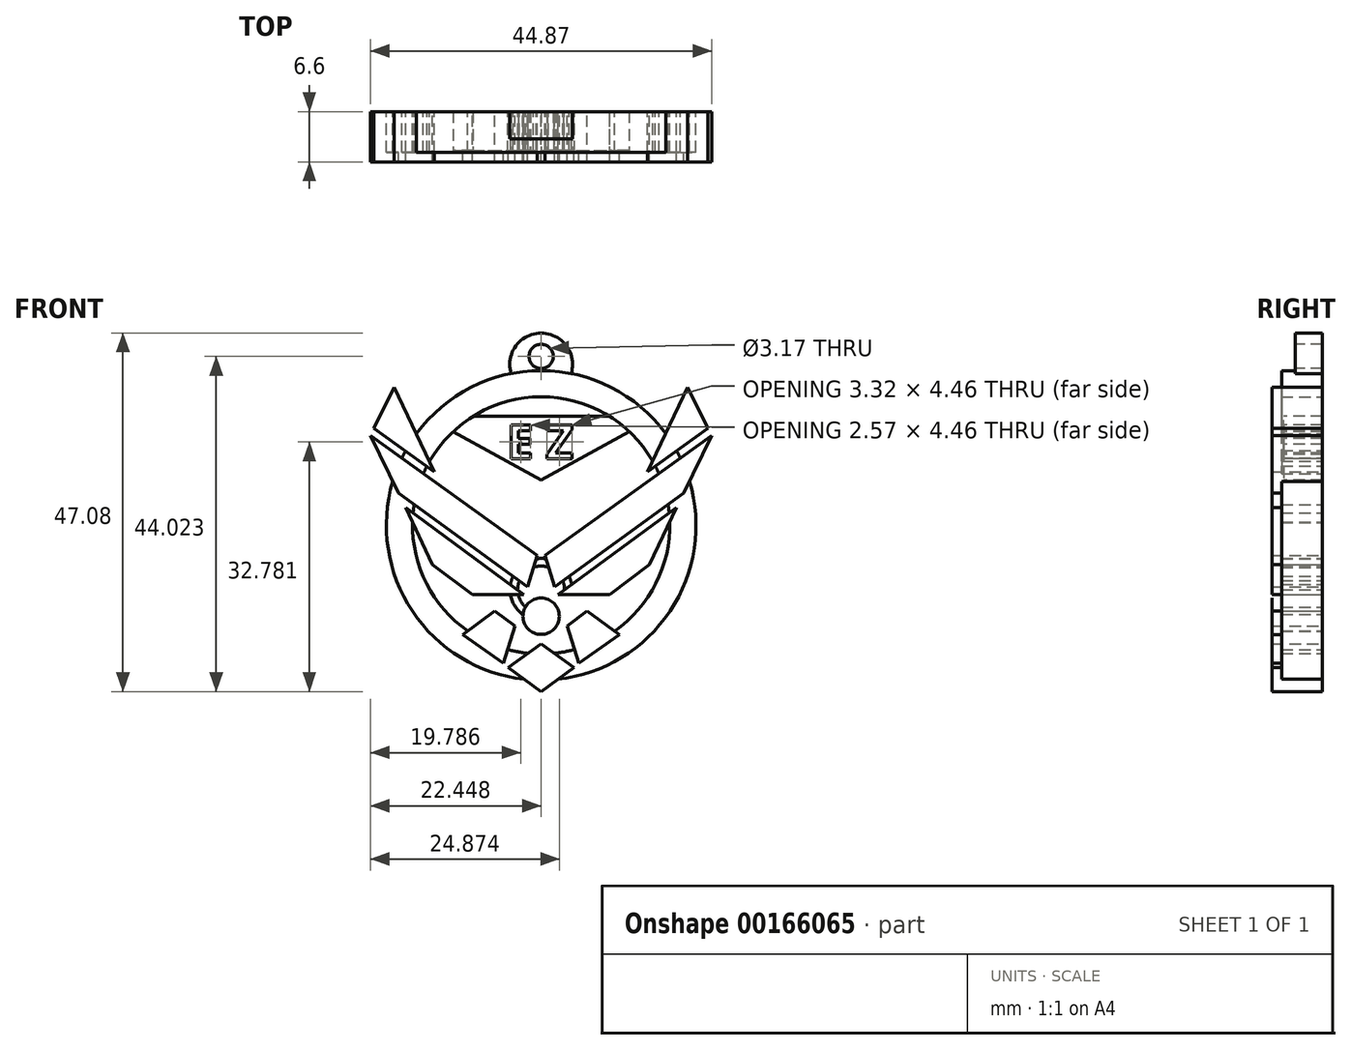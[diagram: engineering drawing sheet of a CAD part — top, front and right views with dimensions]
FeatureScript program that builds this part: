
annotation { "Feature Type Name" : "Feature", "Feature Type Description" : "" }
export const myFeature = defineFeature(function(context is Context, id is Id, definition is map)
    precondition{}
    {
        {
            var Q0;
            Q0=qCreatedBy(makeId("Front.planeOp"),FACE);
            var sketch = newSketch(context, id + "F0", { "sketchPlane" : qUnion([Q0])});
            skLineSegment(sketch, "E0", {"start": v(-11.75, -13.54) * mm, "end": v(-7.45, -10.45) * mm});
            skLineSegment(sketch, "E1", {"start": v(-11.75, -13.54) * mm, "end": v(-7.45, -16.7) * mm});
            skArc(sketch, "E2", {"start": v(-7.43, -4.4) * mm, "mid": v(-9.82, -6.8) * mm, "end": v(-7.43, -9.2) * mm});
            skLineSegment(sketch, "E3", {"start": v(-13.5, -6.12) * mm, "end": v(-10.86, -8.08) * mm});
            skLineSegment(sketch, "E4", {"start": v(-10.86, -8.08) * mm, "end": v(-12.4, -12.94) * mm});
            skLineSegment(sketch, "E5", {"start": v(-12.4, -12.94) * mm, "end": v(-17.74, -9.24) * mm});
            skLineSegment(sketch, "E6", {"start": v(-17.74, -9.24) * mm, "end": v(-13.5, -6.12) * mm});
            skLineSegment(sketch, "E7", {"start": v(-25.25, 7.48) * mm, "end": v(-21.7, 0) * mm});
            skLineSegment(sketch, "E8", {"start": v(-21.7, 0) * mm, "end": v(-16.47, -3.95) * mm});
            skLineSegment(sketch, "E9", {"start": v(-16.47, -3.95) * mm, "end": v(-9.7, -3.95) * mm});
            skLineSegment(sketch, "E10", {"start": v(-9.7, -3.95) * mm, "end": v(-25.25, 7.48) * mm});
            skLineSegment(sketch, "E11", {"start": v(-29.88, 16.94) * mm, "end": v(-7.95, 1.18) * mm});
            skLineSegment(sketch, "E12", {"start": v(-7.95, 1.18) * mm, "end": v(-9.22, -2.92) * mm});
            skLineSegment(sketch, "E13", {"start": v(-9.22, -2.92) * mm, "end": v(-26.2, 9.35) * mm});
            skLineSegment(sketch, "E14", {"start": v(-26.2, 9.35) * mm, "end": v(-29.88, 16.94) * mm});
            skLineSegment(sketch, "E15", {"start": v(-29.39, 17.92) * mm, "end": v(-21.44, 12.2) * mm});
            skLineSegment(sketch, "E16", {"start": v(-21.44, 12.2) * mm, "end": v(-26.72, 23.3) * mm});
            skLineSegment(sketch, "E17", {"start": v(-26.72, 23.3) * mm, "end": v(-29.39, 17.92) * mm});
            skArc(sketch, "E18.MirrorCS", {"start": v(-7.45, -4.4) * mm, "mid": v(-5.05, -6.8) * mm, "end": v(-7.45, -9.2) * mm});
            skLineSegment(sketch, "E19.MirrorCS", {"start": v(-3.14, -13.54) * mm, "end": v(-7.45, -10.45) * mm});
            skLineSegment(sketch, "E20.MirrorCS", {"start": v(-3.14, -13.54) * mm, "end": v(-7.45, -16.7) * mm});
            skLineSegment(sketch, "E21.MirrorCS", {"start": v(-5.67, -2.92) * mm, "end": v(11.3, 9.35) * mm});
            skLineSegment(sketch, "E22.MirrorCS", {"start": v(14.5, 17.92) * mm, "end": v(6.55, 12.2) * mm});
            skLineSegment(sketch, "E23.MirrorCS", {"start": v(11.83, 23.3) * mm, "end": v(14.5, 17.92) * mm});
            skLineSegment(sketch, "E24.MirrorCS", {"start": v(10.36, 7.48) * mm, "end": v(6.81, 0) * mm});
            skLineSegment(sketch, "E25.MirrorCS", {"start": v(2.85, -9.24) * mm, "end": v(-1.39, -6.12) * mm});
            skLineSegment(sketch, "E26.MirrorCS", {"start": v(-2.5, -12.94) * mm, "end": v(2.85, -9.24) * mm});
            skLineSegment(sketch, "E27.MirrorCS", {"start": v(-4.03, -8.08) * mm, "end": v(-2.5, -12.94) * mm});
            skLineSegment(sketch, "E28.MirrorCS", {"start": v(-1.39, -6.12) * mm, "end": v(-4.03, -8.08) * mm});
            skLineSegment(sketch, "E29.MirrorCS", {"start": v(-5.2, -3.95) * mm, "end": v(10.36, 7.48) * mm});
            skLineSegment(sketch, "E30.MirrorCS", {"start": v(1.58, -3.95) * mm, "end": v(-5.2, -3.95) * mm});
            skLineSegment(sketch, "E31.MirrorCS", {"start": v(6.81, 0) * mm, "end": v(1.58, -3.95) * mm});
            skLineSegment(sketch, "E32.MirrorCS", {"start": v(6.55, 12.2) * mm, "end": v(11.83, 23.3) * mm});
            skLineSegment(sketch, "E33.MirrorCS", {"start": v(11.3, 9.35) * mm, "end": v(14.99, 16.94) * mm});
            skLineSegment(sketch, "E34.MirrorCS", {"start": v(14.99, 16.94) * mm, "end": v(-6.94, 1.18) * mm});
            skLineSegment(sketch, "E35.MirrorCS", {"start": v(-6.94, 1.18) * mm, "end": v(-5.67, -2.92) * mm});
            skCircle(sketch, "E36", {"center": v(-7.43, 5.14) * mm, "radius": 20.33 * mm});
            skCircle(sketch, "E37", {"center": v(-7.43, 5.14) * mm, "radius": 16.9 * mm});
            skCircle(sketch, "E38", {"center": v(-7.44, -3.28) * mm, "radius": 4.07 * mm});
            skCircle(sketch, "E39", {"center": v(-7.44, -3.28) * mm, "radius": 3.07 * mm});
            skCircle(sketch, "E40", {"center": v(-7.43, 26.27) * mm, "radius": 4.13 * mm});
            skCircle(sketch, "E41", {"center": v(-7.43, 27.33) * mm, "radius": 1.59 * mm});
            skText(sketch, "E42", { "text": "E Z", "fontName": "OpenSans-Bold.ttf"});
            skLineSegment(sketch, "E43", {"start": v(-7.44, 18.9) * mm, "end": v(-7.44, 13.47) * mm});
            skLineSegment(sketch, "E44", {"start": v(-19, 17.46) * mm, "end": v(-7.44, 11.07) * mm});
            skLineSegment(sketch, "E45", {"start": v(-7.44, 11.07) * mm, "end": v(4.13, 17.46) * mm});
            skLineSegment(sketch, "E46", {"start": v(-16.38, 19.47) * mm, "end": v(1.52, 19.47) * mm});
            const initialGuessF0  = {"E42": [-0.01194, 0.01386, 1, 0, 0.0045]};
            skSetInitialGuess(sketch, initialGuessF0);
            skSolve(sketch);
        }
        {
            var Q0;
            {var subQ0=sQuery(id+"F0.wireOp",EDGE,"E17");Q0=makeQuery(id+"F0.imprint","IMPRINT",FACE,{"disambiguationData":[TD([[makeQuery(id+"F0.imprint","IMPRINT",EDGE,{"derivedFrom":subQ0}),1.0]])]});}
            var Q1;
            {var subQ0=sQuery(id+"F0.wireOp",EDGE,"E36");var subQ1=sQuery(id+"F0.wireOp",EDGE,"E15");var subQ2=makeQuery(id+"F0.imprint","INTERSECT",VERTEX,{"derivedFrom":[subQ1,subQ0]});Q1=makeQuery(id+"F0.imprint","IMPRINT",FACE,{"disambiguationData":[TD([[makeQuery(id+"F0.imprint","IMPRINT",EDGE,{"disambiguationData":[TD([[subQ2,-1.0]])],"derivedFrom":subQ1}),1.0]])]});}
            var Q2;
            {var subQ0=sQuery(id+"F0.wireOp",EDGE,"E16");var subQ1=sQuery(id+"F0.wireOp",EDGE,"E15");var subQ2=makeQuery(id+"F0.imprint","INTERSECT",VERTEX,{"derivedFrom":[subQ1,subQ0]});Q2=makeQuery(id+"F0.imprint","IMPRINT",FACE,{"disambiguationData":[TD([[makeQuery(id+"F0.imprint","IMPRINT",EDGE,{"disambiguationData":[TD([[subQ2,1.0]])],"derivedFrom":subQ1}),1.0]])]});}
            var Q3;
            {var subQ1=sQuery(id+"F0.wireOp",EDGE,"E11");var subQ7=sQuery(id+"F0.wireOp",EDGE,"E36");var subQ9=makeQuery(id+"F0.imprint","INTERSECT",VERTEX,{"derivedFrom":[subQ1,subQ7]});Q3=makeQuery(id+"F0.imprint","IMPRINT",FACE,{"disambiguationData":[TD([[makeQuery(id+"F0.imprint","IMPRINT",EDGE,{"disambiguationData":[TD([[subQ9,-1.0]])],"derivedFrom":subQ1}),-1.0]])]});}
            var Q4;
            {var subQ0=sQuery(id+"F0.wireOp",EDGE,"E14");var subQ1=sQuery(id+"F0.wireOp",EDGE,"E11");var subQ2=makeQuery(id+"F0.imprint","INTERSECT",VERTEX,{"derivedFrom":[subQ1,subQ0]});Q4=makeQuery(id+"F0.imprint","IMPRINT",FACE,{"disambiguationData":[TD([[makeQuery(id+"F0.imprint","IMPRINT",EDGE,{"disambiguationData":[TD([[subQ2,-1.0]])],"derivedFrom":subQ1}),-1.0]])]});}
            var Q5;
            {var subQ0=sQuery(id+"F0.wireOp",EDGE,"E12");Q5=makeQuery(id+"F0.imprint","IMPRINT",FACE,{"disambiguationData":[TD([[makeQuery(id+"F0.imprint","IMPRINT",EDGE,{"derivedFrom":subQ0}),-1.0]])]});}
            var Q6;
            {var subQ4=sQuery(id+"F0.wireOp",EDGE,"E8");Q6=makeQuery(id+"F0.imprint","IMPRINT",FACE,{"disambiguationData":[TD([[makeQuery(id+"F0.imprint","IMPRINT",EDGE,{"derivedFrom":subQ4}),1.0]])]});}
            var Q7;
            {var subQ5=sQuery(id+"F0.wireOp",EDGE,"E3");Q7=makeQuery(id+"F0.imprint","IMPRINT",FACE,{"disambiguationData":[TD([[makeQuery(id+"F0.imprint","IMPRINT",EDGE,{"derivedFrom":subQ5}),-1.0]])]});}
            var Q8;
            {var subQ0=sQuery(id+"F0.wireOp",EDGE,"E19.MirrorCS");var subQ1=sQuery(id+"F0.wireOp",EDGE,"E0");var subQ2=makeQuery(id+"F0.imprint","INTERSECT",VERTEX,{"derivedFrom":[subQ1,subQ0]});Q8=makeQuery(id+"F0.imprint","IMPRINT",FACE,{"disambiguationData":[TD([[makeQuery(id+"F0.imprint","IMPRINT",EDGE,{"disambiguationData":[TD([[subQ2,1.0]])],"derivedFrom":subQ1}),-1.0]])]});}
            var Q9;
            {var subQ7=sQuery(id+"F0.wireOp",EDGE,"E1");var subQ8=sQuery(id+"F0.wireOp",EDGE,"E0");var subQ9=makeQuery(id+"F0.imprint","INTERSECT",VERTEX,{"derivedFrom":[subQ8,subQ7]});Q9=makeQuery(id+"F0.imprint","IMPRINT",FACE,{"disambiguationData":[TD([[makeQuery(id+"F0.imprint","IMPRINT",EDGE,{"disambiguationData":[TD([[subQ9,-1.0]])],"derivedFrom":subQ8}),-1.0]])]});}
            var Q10;
            {var subQ0=sQuery(id+"F0.wireOp",EDGE,"E5");var subQ1=sQuery(id+"F0.wireOp",EDGE,"E4");var subQ2=makeQuery(id+"F0.imprint","INTERSECT",VERTEX,{"derivedFrom":[subQ1,subQ0]});Q10=makeQuery(id+"F0.imprint","IMPRINT",FACE,{"disambiguationData":[TD([[makeQuery(id+"F0.imprint","IMPRINT",EDGE,{"disambiguationData":[TD([[subQ2,1.0]])],"derivedFrom":subQ1}),-1.0]])]});}
            var Q11;
            {var subQ5=sQuery(id+"F0.wireOp",EDGE,"E25.MirrorCS");Q11=makeQuery(id+"F0.imprint","IMPRINT",FACE,{"disambiguationData":[TD([[makeQuery(id+"F0.imprint","IMPRINT",EDGE,{"derivedFrom":subQ5}),1.0]])]});}
            var Q12;
            {var subQ0=sQuery(id+"F0.wireOp",EDGE,"E27.MirrorCS");var subQ1=sQuery(id+"F0.wireOp",EDGE,"E26.MirrorCS");var subQ2=makeQuery(id+"F0.imprint","INTERSECT",VERTEX,{"derivedFrom":[subQ1,subQ0]});Q12=makeQuery(id+"F0.imprint","IMPRINT",FACE,{"disambiguationData":[TD([[makeQuery(id+"F0.imprint","IMPRINT",EDGE,{"disambiguationData":[TD([[subQ2,-1.0]])],"derivedFrom":subQ1}),1.0]])]});}
            var Q13;
            {var subQ0=sQuery(id+"F0.wireOp",EDGE,"E20.MirrorCS");var subQ1=sQuery(id+"F0.wireOp",EDGE,"E1");var subQ2=makeQuery(id+"F0.imprint","INTERSECT",VERTEX,{"derivedFrom":[subQ1,subQ0]});Q13=makeQuery(id+"F0.imprint","IMPRINT",FACE,{"disambiguationData":[TD([[makeQuery(id+"F0.imprint","IMPRINT",EDGE,{"disambiguationData":[TD([[subQ2,1.0]])],"derivedFrom":subQ1}),1.0]])]});}
            var Q14;
            {var subQ1=sQuery(id+"F0.wireOp",EDGE,"E30.MirrorCS");Q14=makeQuery(id+"F0.imprint","IMPRINT",FACE,{"disambiguationData":[TD([[makeQuery(id+"F0.imprint","IMPRINT",EDGE,{"derivedFrom":subQ1}),-1.0]])]});}
            var Q15;
            {var subQ0=sQuery(id+"F0.wireOp",EDGE,"E35.MirrorCS");Q15=makeQuery(id+"F0.imprint","IMPRINT",FACE,{"disambiguationData":[TD([[makeQuery(id+"F0.imprint","IMPRINT",EDGE,{"derivedFrom":subQ0}),1.0]])]});}
            var Q16;
            {var subQ1=sQuery(id+"F0.wireOp",EDGE,"E21.MirrorCS");var subQ7=sQuery(id+"F0.wireOp",EDGE,"E33.MirrorCS");var subQ8=makeQuery(id+"F0.imprint","INTERSECT",VERTEX,{"derivedFrom":[subQ1,subQ7]});Q16=makeQuery(id+"F0.imprint","IMPRINT",FACE,{"disambiguationData":[TD([[makeQuery(id+"F0.imprint","IMPRINT",EDGE,{"disambiguationData":[TD([[subQ8,1.0]])],"derivedFrom":subQ1}),1.0]])]});}
            var Q17;
            {var subQ0=sQuery(id+"F0.wireOp",EDGE,"E34.MirrorCS");var subQ1=sQuery(id+"F0.wireOp",EDGE,"E33.MirrorCS");var subQ2=makeQuery(id+"F0.imprint","INTERSECT",VERTEX,{"derivedFrom":[subQ1,subQ0]});Q17=makeQuery(id+"F0.imprint","IMPRINT",FACE,{"disambiguationData":[TD([[makeQuery(id+"F0.imprint","IMPRINT",EDGE,{"disambiguationData":[TD([[subQ2,1.0]])],"derivedFrom":subQ1}),1.0]])]});}
            var Q18;
            {var subQ0=sQuery(id+"F0.wireOp",EDGE,"E23.MirrorCS");Q18=makeQuery(id+"F0.imprint","IMPRINT",FACE,{"disambiguationData":[TD([[makeQuery(id+"F0.imprint","IMPRINT",EDGE,{"derivedFrom":subQ0}),-1.0]])]});}
            var Q19;
            {var subQ0=sQuery(id+"F0.wireOp",EDGE,"E36");var subQ1=sQuery(id+"F0.wireOp",EDGE,"E22.MirrorCS");var subQ2=makeQuery(id+"F0.imprint","INTERSECT",VERTEX,{"derivedFrom":[subQ1,subQ0]});Q19=makeQuery(id+"F0.imprint","IMPRINT",FACE,{"disambiguationData":[TD([[makeQuery(id+"F0.imprint","IMPRINT",EDGE,{"disambiguationData":[TD([[subQ2,-1.0]])],"derivedFrom":subQ1}),-1.0]])]});}
            var Q20;
            {var subQ0=sQuery(id+"F0.wireOp",EDGE,"E32.MirrorCS");var subQ1=sQuery(id+"F0.wireOp",EDGE,"E22.MirrorCS");var subQ2=makeQuery(id+"F0.imprint","INTERSECT",VERTEX,{"derivedFrom":[subQ1,subQ0]});Q20=makeQuery(id+"F0.imprint","IMPRINT",FACE,{"disambiguationData":[TD([[makeQuery(id+"F0.imprint","IMPRINT",EDGE,{"disambiguationData":[TD([[subQ2,1.0]])],"derivedFrom":subQ1}),-1.0]])]});}
            var Q21;
            Q21=makeQuery(id+"F0.imprint","IMPRINT",FACE,{"disambiguationData":[TD([[makeQuery(id+"F0.imprint","IMPRINT",EDGE,{"derivedFrom":sQuery(id+"F0.wireOp",EDGE,"E2")}),1.0]])]});
            var Q22;
            {var subQ0=sQuery(id+"F0.wireOp",EDGE,"E10");var subQ1=sQuery(id+"F0.wireOp",EDGE,"E7");var subQ2=makeQuery(id+"F0.imprint","INTERSECT",VERTEX,{"derivedFrom":[subQ1,subQ0]});Q22=makeQuery(id+"F0.imprint","IMPRINT",FACE,{"disambiguationData":[TD([[makeQuery(id+"F0.imprint","IMPRINT",EDGE,{"disambiguationData":[TD([[subQ2,-1.0]])],"derivedFrom":subQ1}),1.0]])]});}
            var Q23;
            {var subQ0=sQuery(id+"F0.wireOp",EDGE,"E29.MirrorCS");var subQ1=sQuery(id+"F0.wireOp",EDGE,"E24.MirrorCS");var subQ2=makeQuery(id+"F0.imprint","INTERSECT",VERTEX,{"derivedFrom":[subQ1,subQ0]});Q23=makeQuery(id+"F0.imprint","IMPRINT",FACE,{"disambiguationData":[TD([[makeQuery(id+"F0.imprint","IMPRINT",EDGE,{"disambiguationData":[TD([[subQ2,-1.0]])],"derivedFrom":subQ1}),-1.0]])]});}
            var Q24;
            {var subQ1=sQuery(id+"F0.wireOp",EDGE,"E11");var subQ7=sQuery(id+"F0.wireOp",EDGE,"E12");var subQ8=makeQuery(id+"F0.imprint","INTERSECT",VERTEX,{"derivedFrom":[subQ1,subQ7]});Q24=makeQuery(id+"F0.imprint","IMPRINT",FACE,{"disambiguationData":[TD([[makeQuery(id+"F0.imprint","IMPRINT",EDGE,{"disambiguationData":[TD([[subQ8,1.0]])],"derivedFrom":subQ1}),-1.0]])]});}
            var Q25;
            {var subQ0=sQuery(id+"F0.wireOp",EDGE,"E38");var subQ1=sQuery(id+"F0.wireOp",EDGE,"E12");var subQ2=makeQuery(id+"F0.imprint","INTERSECT",VERTEX,{"derivedFrom":[subQ1,subQ0]});Q25=makeQuery(id+"F0.imprint","IMPRINT",FACE,{"disambiguationData":[TD([[makeQuery(id+"F0.imprint","IMPRINT",EDGE,{"disambiguationData":[TD([[subQ2,-1.0]])],"derivedFrom":subQ1}),-1.0]])]});}
            var Q26;
            {var subQ0=sQuery(id+"F0.wireOp",EDGE,"E38");var subQ1=sQuery(id+"F0.wireOp",EDGE,"E9");var subQ2=makeQuery(id+"F0.imprint","INTERSECT",VERTEX,{"derivedFrom":[subQ1,subQ0]});Q26=makeQuery(id+"F0.imprint","IMPRINT",FACE,{"disambiguationData":[TD([[makeQuery(id+"F0.imprint","IMPRINT",EDGE,{"disambiguationData":[TD([[subQ2,-1.0]])],"derivedFrom":subQ1}),1.0]])]});}
            var Q27;
            {var subQ0=sQuery(id+"F0.wireOp",EDGE,"E10");var subQ1=sQuery(id+"F0.wireOp",EDGE,"E9");var subQ2=makeQuery(id+"F0.imprint","INTERSECT",VERTEX,{"derivedFrom":[subQ1,subQ0]});Q27=makeQuery(id+"F0.imprint","IMPRINT",FACE,{"disambiguationData":[TD([[makeQuery(id+"F0.imprint","IMPRINT",EDGE,{"disambiguationData":[TD([[subQ2,1.0]])],"derivedFrom":subQ1}),1.0]])]});}
            var Q28;
            {var subQ0=sQuery(id+"F0.wireOp",EDGE,"E39");var subQ1=sQuery(id+"F0.wireOp",EDGE,"E2");var subQ2=makeQuery(id+"F0.imprint","INTERSECT",VERTEX,{"derivedFrom":[subQ1,subQ0]});Q28=makeQuery(id+"F0.imprint","IMPRINT",FACE,{"disambiguationData":[TD([[makeQuery(id+"F0.imprint","IMPRINT",EDGE,{"disambiguationData":[TD([[subQ2,-1.0]])],"derivedFrom":subQ1}),1.0]])]});}
            var Q29;
            {var subQ0=sQuery(id+"F0.wireOp",EDGE,"E39");var subQ1=sQuery(id+"F0.wireOp",EDGE,"E29.MirrorCS");var subQ2=makeQuery(id+"F0.imprint","INTERSECT",VERTEX,{"derivedFrom":[subQ1,subQ0]});Q29=makeQuery(id+"F0.imprint","IMPRINT",FACE,{"disambiguationData":[TD([[makeQuery(id+"F0.imprint","IMPRINT",EDGE,{"disambiguationData":[TD([[subQ2,-1.0]])],"derivedFrom":subQ1}),-1.0]])]});}
            var Q30;
            {var subQ0=sQuery(id+"F0.wireOp",EDGE,"E31.MirrorCS");Q30=makeQuery(id+"F0.imprint","IMPRINT",FACE,{"disambiguationData":[TD([[makeQuery(id+"F0.imprint","IMPRINT",EDGE,{"derivedFrom":subQ0}),-1.0]])]});}
            var Q31;
            {var subQ0=sQuery(id+"F0.wireOp",EDGE,"E39");var subQ1=sQuery(id+"F0.wireOp",EDGE,"E21.MirrorCS");var subQ2=makeQuery(id+"F0.imprint","INTERSECT",VERTEX,{"derivedFrom":[subQ1,subQ0]});Q31=makeQuery(id+"F0.imprint","IMPRINT",FACE,{"disambiguationData":[TD([[makeQuery(id+"F0.imprint","IMPRINT",EDGE,{"disambiguationData":[TD([[subQ2,-1.0]])],"derivedFrom":subQ1}),1.0]])]});}
            var Q32;
            {var subQ1=sQuery(id+"F0.wireOp",EDGE,"E21.MirrorCS");var subQ7=sQuery(id+"F0.wireOp",EDGE,"E38");var subQ9=makeQuery(id+"F0.imprint","INTERSECT",VERTEX,{"derivedFrom":[subQ1,subQ7]});Q32=makeQuery(id+"F0.imprint","IMPRINT",FACE,{"disambiguationData":[TD([[makeQuery(id+"F0.imprint","IMPRINT",EDGE,{"disambiguationData":[TD([[subQ9,-1.0]])],"derivedFrom":subQ1}),1.0]])]});}
            extrude(context, id + "F1", {"entities" : qUnion([Q0, Q1, Q2, Q3, Q4, Q5, Q6, Q7, Q8, Q9, Q10, Q11, Q12, Q13, Q14, Q15, Q16, Q17, Q18, Q19, Q20, Q21, Q22, Q23, Q24, Q25, Q26, Q27, Q28, Q29, Q30, Q31, Q32]), "depth" : 1.52 * mm});
        }
        {
            var Q0;
            {var subQ0=sQuery(id+"F0.wireOp",EDGE,"E36");var subQ1=sQuery(id+"F0.wireOp",EDGE,"E16");var subQ2=makeQuery(id+"F0.imprint","INTERSECT",VERTEX,{"derivedFrom":[subQ1,subQ0]});Q0=makeQuery(id+"F0.imprint","IMPRINT",FACE,{"disambiguationData":[TD([[makeQuery(id+"F0.imprint","IMPRINT",EDGE,{"disambiguationData":[TD([[subQ2,1.0]])],"derivedFrom":subQ1}),-1.0]])]});}
            var Q1;
            {var subQ0=sQuery(id+"F0.wireOp",EDGE,"E36");var subQ1=sQuery(id+"F0.wireOp",EDGE,"E22.MirrorCS");var subQ2=makeQuery(id+"F0.imprint","INTERSECT",VERTEX,{"derivedFrom":[subQ1,subQ0]});Q1=makeQuery(id+"F0.imprint","IMPRINT",FACE,{"disambiguationData":[TD([[makeQuery(id+"F0.imprint","IMPRINT",EDGE,{"disambiguationData":[TD([[subQ2,-1.0]])],"derivedFrom":subQ1}),1.0]])]});}
            var Q2;
            {var subQ0=sQuery(id+"F0.wireOp",EDGE,"E36");var subQ1=sQuery(id+"F0.wireOp",EDGE,"E22.MirrorCS");var subQ2=makeQuery(id+"F0.imprint","INTERSECT",VERTEX,{"derivedFrom":[subQ1,subQ0]});Q2=makeQuery(id+"F0.imprint","IMPRINT",FACE,{"disambiguationData":[TD([[makeQuery(id+"F0.imprint","IMPRINT",EDGE,{"disambiguationData":[TD([[subQ2,-1.0]])],"derivedFrom":subQ1}),-1.0]])]});}
            var Q3;
            {var subQ1=sQuery(id+"F0.wireOp",EDGE,"E21.MirrorCS");var subQ7=sQuery(id+"F0.wireOp",EDGE,"E33.MirrorCS");var subQ8=makeQuery(id+"F0.imprint","INTERSECT",VERTEX,{"derivedFrom":[subQ1,subQ7]});Q3=makeQuery(id+"F0.imprint","IMPRINT",FACE,{"disambiguationData":[TD([[makeQuery(id+"F0.imprint","IMPRINT",EDGE,{"disambiguationData":[TD([[subQ8,1.0]])],"derivedFrom":subQ1}),1.0]])]});}
            var Q4;
            {var subQ1=sQuery(id+"F0.wireOp",EDGE,"E19.MirrorCS");var subQ15=sQuery(id+"F0.wireOp",EDGE,"E20.MirrorCS");var subQ16=makeQuery(id+"F0.imprint","INTERSECT",VERTEX,{"derivedFrom":[subQ1,subQ15]});Q4=makeQuery(id+"F0.imprint","IMPRINT",FACE,{"disambiguationData":[TD([[makeQuery(id+"F0.imprint","IMPRINT",EDGE,{"disambiguationData":[TD([[subQ16,-1.0]])],"derivedFrom":subQ1}),-1.0]])]});}
            var Q5;
            {var subQ10=sQuery(id+"F0.wireOp",EDGE,"E1");var subQ11=sQuery(id+"F0.wireOp",EDGE,"E0");var subQ12=makeQuery(id+"F0.imprint","INTERSECT",VERTEX,{"derivedFrom":[subQ11,subQ10]});Q5=makeQuery(id+"F0.imprint","IMPRINT",FACE,{"disambiguationData":[TD([[makeQuery(id+"F0.imprint","IMPRINT",EDGE,{"disambiguationData":[TD([[subQ12,-1.0]])],"derivedFrom":subQ11}),1.0]])]});}
            var Q6;
            {var subQ0=sQuery(id+"F0.wireOp",EDGE,"E36");var subQ1=sQuery(id+"F0.wireOp",EDGE,"E15");var subQ2=makeQuery(id+"F0.imprint","INTERSECT",VERTEX,{"derivedFrom":[subQ1,subQ0]});Q6=makeQuery(id+"F0.imprint","IMPRINT",FACE,{"disambiguationData":[TD([[makeQuery(id+"F0.imprint","IMPRINT",EDGE,{"disambiguationData":[TD([[subQ2,-1.0]])],"derivedFrom":subQ1}),1.0]])]});}
            var Q7;
            {var subQ0=sQuery(id+"F0.wireOp",EDGE,"E36");var subQ1=sQuery(id+"F0.wireOp",EDGE,"E11");var subQ2=makeQuery(id+"F0.imprint","INTERSECT",VERTEX,{"derivedFrom":[subQ1,subQ0]});Q7=makeQuery(id+"F0.imprint","IMPRINT",FACE,{"disambiguationData":[TD([[makeQuery(id+"F0.imprint","IMPRINT",EDGE,{"disambiguationData":[TD([[subQ2,-1.0]])],"derivedFrom":subQ1}),1.0]])]});}
            var Q8;
            {var subQ1=sQuery(id+"F0.wireOp",EDGE,"E11");var subQ7=sQuery(id+"F0.wireOp",EDGE,"E36");var subQ9=makeQuery(id+"F0.imprint","INTERSECT",VERTEX,{"derivedFrom":[subQ1,subQ7]});Q8=makeQuery(id+"F0.imprint","IMPRINT",FACE,{"disambiguationData":[TD([[makeQuery(id+"F0.imprint","IMPRINT",EDGE,{"disambiguationData":[TD([[subQ9,-1.0]])],"derivedFrom":subQ1}),-1.0]])]});}
            var Q9;
            {var subQ7=sQuery(id+"F0.wireOp",EDGE,"E1");var subQ8=sQuery(id+"F0.wireOp",EDGE,"E0");var subQ9=makeQuery(id+"F0.imprint","INTERSECT",VERTEX,{"derivedFrom":[subQ8,subQ7]});Q9=makeQuery(id+"F0.imprint","IMPRINT",FACE,{"disambiguationData":[TD([[makeQuery(id+"F0.imprint","IMPRINT",EDGE,{"disambiguationData":[TD([[subQ9,-1.0]])],"derivedFrom":subQ8}),-1.0]])]});}
            var Q10;
            {var subQ0=sQuery(id+"F0.wireOp",EDGE,"E38");var subQ1=sQuery(id+"F0.wireOp",EDGE,"E12");var subQ2=makeQuery(id+"F0.imprint","INTERSECT",VERTEX,{"derivedFrom":[subQ1,subQ0]});Q10=makeQuery(id+"F0.imprint","IMPRINT",FACE,{"disambiguationData":[TD([[makeQuery(id+"F0.imprint","IMPRINT",EDGE,{"disambiguationData":[TD([[subQ2,-1.0]])],"derivedFrom":subQ1}),1.0]])]});}
            var Q11;
            {var subQ0=sQuery(id+"F0.wireOp",EDGE,"E39");var subQ1=sQuery(id+"F0.wireOp",EDGE,"E10");var subQ2=makeQuery(id+"F0.imprint","INTERSECT",VERTEX,{"derivedFrom":[subQ1,subQ0]});Q11=makeQuery(id+"F0.imprint","IMPRINT",FACE,{"disambiguationData":[TD([[makeQuery(id+"F0.imprint","IMPRINT",EDGE,{"disambiguationData":[TD([[subQ2,-1.0]])],"derivedFrom":subQ1}),-1.0]])]});}
            var Q12;
            {var subQ0=sQuery(id+"F0.wireOp",EDGE,"E39");var subQ1=sQuery(id+"F0.wireOp",EDGE,"E2");var subQ2=makeQuery(id+"F0.imprint","INTERSECT",VERTEX,{"derivedFrom":[subQ1,subQ0]});Q12=makeQuery(id+"F0.imprint","IMPRINT",FACE,{"disambiguationData":[TD([[makeQuery(id+"F0.imprint","IMPRINT",EDGE,{"disambiguationData":[TD([[subQ2,-1.0]])],"derivedFrom":subQ1}),-1.0]])]});}
            var Q13;
            {var subQ0=sQuery(id+"F0.wireOp",EDGE,"E39");var subQ1=sQuery(id+"F0.wireOp",EDGE,"E18.MirrorCS");var subQ2=makeQuery(id+"F0.imprint","INTERSECT",VERTEX,{"derivedFrom":[subQ1,subQ0]});Q13=makeQuery(id+"F0.imprint","IMPRINT",FACE,{"disambiguationData":[TD([[makeQuery(id+"F0.imprint","IMPRINT",EDGE,{"disambiguationData":[TD([[subQ2,-1.0]])],"derivedFrom":subQ1}),1.0]])]});}
            var Q14;
            {var subQ0=sQuery(id+"F0.wireOp",EDGE,"E39");var subQ1=sQuery(id+"F0.wireOp",EDGE,"E21.MirrorCS");var subQ2=makeQuery(id+"F0.imprint","INTERSECT",VERTEX,{"derivedFrom":[subQ1,subQ0]});Q14=makeQuery(id+"F0.imprint","IMPRINT",FACE,{"disambiguationData":[TD([[makeQuery(id+"F0.imprint","IMPRINT",EDGE,{"disambiguationData":[TD([[subQ2,-1.0]])],"derivedFrom":subQ1}),-1.0]])]});}
            var Q15;
            {var subQ0=sQuery(id+"F0.wireOp",EDGE,"E36");var subQ1=sQuery(id+"F0.wireOp",EDGE,"E32.MirrorCS");var subQ2=makeQuery(id+"F0.imprint","INTERSECT",VERTEX,{"derivedFrom":[subQ1,subQ0]});Q15=makeQuery(id+"F0.imprint","IMPRINT",FACE,{"disambiguationData":[TD([[makeQuery(id+"F0.imprint","IMPRINT",EDGE,{"disambiguationData":[TD([[subQ2,1.0]])],"derivedFrom":subQ1}),1.0]])]});}
            var Q16;
            {var subQ0=sQuery(id+"F0.wireOp",EDGE,"E40");var subQ1=sQuery(id+"F0.wireOp",EDGE,"E36");var subQ2=makeQuery(id+"F0.imprint","INTERSECT",VERTEX,{"disambiguationData":[OD(0.0)],"derivedFrom":[subQ1,subQ0]});Q16=makeQuery(id+"F0.imprint","IMPRINT",FACE,{"disambiguationData":[TD([[makeQuery(id+"F0.imprint","IMPRINT",EDGE,{"disambiguationData":[TD([[subQ2,-1.0]])],"derivedFrom":subQ1}),1.0]])]});}
            var Q17;
            {var subQ5=sQuery(id+"F0.wireOp",EDGE,"29c7e069-055f-4118-b34c-edf3fcd1c2af.sketch_text.stroke-1");Q17=makeQuery(id+"F0.imprint","IMPRINT",FACE,{"disambiguationData":[TD([[makeQuery(id+"F0.imprint","IMPRINT",EDGE,{"derivedFrom":subQ5}),1.0]])]});}
            extrude(context, id + "F2", {"entities" : qUnion([Q0, Q1, Q2, Q3, Q4, Q5, Q6, Q7, Q8, Q9, Q10, Q11, Q12, Q13, Q14, Q15, Q16, Q17]), "operationType" : NewBodyOperationType.ADD, "depth" : 0.25 * mm});
        }
        {
            var Q0;
            {var subQ0=sQuery(id+"F0.wireOp",EDGE,"E36");var subQ1=sQuery(id+"F0.wireOp",EDGE,"E16");var subQ2=makeQuery(id+"F0.imprint","INTERSECT",VERTEX,{"derivedFrom":[subQ1,subQ0]});Q0=makeQuery(id+"F0.imprint","IMPRINT",FACE,{"disambiguationData":[TD([[makeQuery(id+"F0.imprint","IMPRINT",EDGE,{"disambiguationData":[TD([[subQ2,1.0]])],"derivedFrom":subQ1}),-1.0]])]});}
            var Q1;
            {var subQ0=sQuery(id+"F0.wireOp",EDGE,"E36");var subQ1=sQuery(id+"F0.wireOp",EDGE,"E22.MirrorCS");var subQ2=makeQuery(id+"F0.imprint","INTERSECT",VERTEX,{"derivedFrom":[subQ1,subQ0]});Q1=makeQuery(id+"F0.imprint","IMPRINT",FACE,{"disambiguationData":[TD([[makeQuery(id+"F0.imprint","IMPRINT",EDGE,{"disambiguationData":[TD([[subQ2,-1.0]])],"derivedFrom":subQ1}),-1.0]])]});}
            var Q2;
            {var subQ0=sQuery(id+"F0.wireOp",EDGE,"E36");var subQ1=sQuery(id+"F0.wireOp",EDGE,"E22.MirrorCS");var subQ2=makeQuery(id+"F0.imprint","INTERSECT",VERTEX,{"derivedFrom":[subQ1,subQ0]});Q2=makeQuery(id+"F0.imprint","IMPRINT",FACE,{"disambiguationData":[TD([[makeQuery(id+"F0.imprint","IMPRINT",EDGE,{"disambiguationData":[TD([[subQ2,-1.0]])],"derivedFrom":subQ1}),1.0]])]});}
            var Q3;
            {var subQ1=sQuery(id+"F0.wireOp",EDGE,"E33.MirrorCS");var subQ7=sQuery(id+"F0.wireOp",EDGE,"E21.MirrorCS");var subQ8=makeQuery(id+"F0.imprint","INTERSECT",VERTEX,{"derivedFrom":[subQ7,subQ1]});Q3=makeQuery(id+"F0.imprint","IMPRINT",FACE,{"disambiguationData":[TD([[makeQuery(id+"F0.imprint","IMPRINT",EDGE,{"disambiguationData":[TD([[subQ8,1.0]])],"derivedFrom":subQ7}),1.0]])]});}
            var Q4;
            {var subQ5=sQuery(id+"F0.wireOp",EDGE,"E26.MirrorCS");Q4=makeQuery(id+"F0.imprint","IMPRINT",FACE,{"disambiguationData":[TD([[makeQuery(id+"F0.imprint","IMPRINT",EDGE,{"derivedFrom":subQ5}),-1.0]])]});}
            var Q5;
            {var subQ7=sQuery(id+"F0.wireOp",EDGE,"E1");var subQ8=sQuery(id+"F0.wireOp",EDGE,"E0");var subQ9=makeQuery(id+"F0.imprint","INTERSECT",VERTEX,{"derivedFrom":[subQ8,subQ7]});Q5=makeQuery(id+"F0.imprint","IMPRINT",FACE,{"disambiguationData":[TD([[makeQuery(id+"F0.imprint","IMPRINT",EDGE,{"disambiguationData":[TD([[subQ9,-1.0]])],"derivedFrom":subQ8}),-1.0]])]});}
            var Q6;
            {var subQ15=sQuery(id+"F0.wireOp",EDGE,"E5");Q6=makeQuery(id+"F0.imprint","IMPRINT",FACE,{"disambiguationData":[TD([[makeQuery(id+"F0.imprint","IMPRINT",EDGE,{"derivedFrom":subQ15}),1.0]])]});}
            var Q7;
            {var subQ5=sQuery(id+"F0.wireOp",EDGE,"E36");var subQ7=sQuery(id+"F0.wireOp",EDGE,"E11");var subQ8=makeQuery(id+"F0.imprint","INTERSECT",VERTEX,{"derivedFrom":[subQ7,subQ5]});Q7=makeQuery(id+"F0.imprint","IMPRINT",FACE,{"disambiguationData":[TD([[makeQuery(id+"F0.imprint","IMPRINT",EDGE,{"disambiguationData":[TD([[subQ8,-1.0]])],"derivedFrom":subQ7}),-1.0]])]});}
            var Q8;
            {var subQ0=sQuery(id+"F0.wireOp",EDGE,"E36");var subQ1=sQuery(id+"F0.wireOp",EDGE,"E11");var subQ2=makeQuery(id+"F0.imprint","INTERSECT",VERTEX,{"derivedFrom":[subQ1,subQ0]});Q8=makeQuery(id+"F0.imprint","IMPRINT",FACE,{"disambiguationData":[TD([[makeQuery(id+"F0.imprint","IMPRINT",EDGE,{"disambiguationData":[TD([[subQ2,-1.0]])],"derivedFrom":subQ1}),1.0]])]});}
            var Q9;
            {var subQ0=sQuery(id+"F0.wireOp",EDGE,"E36");var subQ1=sQuery(id+"F0.wireOp",EDGE,"E15");var subQ2=makeQuery(id+"F0.imprint","INTERSECT",VERTEX,{"derivedFrom":[subQ1,subQ0]});Q9=makeQuery(id+"F0.imprint","IMPRINT",FACE,{"disambiguationData":[TD([[makeQuery(id+"F0.imprint","IMPRINT",EDGE,{"disambiguationData":[TD([[subQ2,-1.0]])],"derivedFrom":subQ1}),1.0]])]});}
            var Q10;
            {var subQ0=sQuery(id+"F0.wireOp",EDGE,"E38");var subQ1=sQuery(id+"F0.wireOp",EDGE,"E12");var subQ2=makeQuery(id+"F0.imprint","INTERSECT",VERTEX,{"derivedFrom":[subQ1,subQ0]});Q10=makeQuery(id+"F0.imprint","IMPRINT",FACE,{"disambiguationData":[TD([[makeQuery(id+"F0.imprint","IMPRINT",EDGE,{"disambiguationData":[TD([[subQ2,-1.0]])],"derivedFrom":subQ1}),1.0]])]});}
            var Q11;
            {var subQ0=sQuery(id+"F0.wireOp",EDGE,"E39");var subQ1=sQuery(id+"F0.wireOp",EDGE,"E21.MirrorCS");var subQ2=makeQuery(id+"F0.imprint","INTERSECT",VERTEX,{"derivedFrom":[subQ1,subQ0]});Q11=makeQuery(id+"F0.imprint","IMPRINT",FACE,{"disambiguationData":[TD([[makeQuery(id+"F0.imprint","IMPRINT",EDGE,{"disambiguationData":[TD([[subQ2,-1.0]])],"derivedFrom":subQ1}),1.0]])]});}
            var Q12;
            {var subQ0=sQuery(id+"F0.wireOp",EDGE,"E39");var subQ1=sQuery(id+"F0.wireOp",EDGE,"E21.MirrorCS");var subQ2=makeQuery(id+"F0.imprint","INTERSECT",VERTEX,{"derivedFrom":[subQ1,subQ0]});Q12=makeQuery(id+"F0.imprint","IMPRINT",FACE,{"disambiguationData":[TD([[makeQuery(id+"F0.imprint","IMPRINT",EDGE,{"disambiguationData":[TD([[subQ2,-1.0]])],"derivedFrom":subQ1}),-1.0]])]});}
            var Q13;
            {var subQ0=sQuery(id+"F0.wireOp",EDGE,"E39");var subQ1=sQuery(id+"F0.wireOp",EDGE,"E18.MirrorCS");var subQ2=makeQuery(id+"F0.imprint","INTERSECT",VERTEX,{"derivedFrom":[subQ1,subQ0]});Q13=makeQuery(id+"F0.imprint","IMPRINT",FACE,{"disambiguationData":[TD([[makeQuery(id+"F0.imprint","IMPRINT",EDGE,{"disambiguationData":[TD([[subQ2,-1.0]])],"derivedFrom":subQ1}),1.0]])]});}
            var Q14;
            {var subQ0=sQuery(id+"F0.wireOp",EDGE,"E39");var subQ1=sQuery(id+"F0.wireOp",EDGE,"E2");var subQ2=makeQuery(id+"F0.imprint","INTERSECT",VERTEX,{"derivedFrom":[subQ1,subQ0]});Q14=makeQuery(id+"F0.imprint","IMPRINT",FACE,{"disambiguationData":[TD([[makeQuery(id+"F0.imprint","IMPRINT",EDGE,{"disambiguationData":[TD([[subQ2,-1.0]])],"derivedFrom":subQ1}),1.0]])]});}
            var Q15;
            {var subQ0=sQuery(id+"F0.wireOp",EDGE,"E39");var subQ1=sQuery(id+"F0.wireOp",EDGE,"E2");var subQ2=makeQuery(id+"F0.imprint","INTERSECT",VERTEX,{"derivedFrom":[subQ1,subQ0]});Q15=makeQuery(id+"F0.imprint","IMPRINT",FACE,{"disambiguationData":[TD([[makeQuery(id+"F0.imprint","IMPRINT",EDGE,{"disambiguationData":[TD([[subQ2,-1.0]])],"derivedFrom":subQ1}),-1.0]])]});}
            var Q16;
            {var subQ0=sQuery(id+"F0.wireOp",EDGE,"E39");var subQ1=sQuery(id+"F0.wireOp",EDGE,"E10");var subQ2=makeQuery(id+"F0.imprint","INTERSECT",VERTEX,{"derivedFrom":[subQ1,subQ0]});Q16=makeQuery(id+"F0.imprint","IMPRINT",FACE,{"disambiguationData":[TD([[makeQuery(id+"F0.imprint","IMPRINT",EDGE,{"disambiguationData":[TD([[subQ2,-1.0]])],"derivedFrom":subQ1}),-1.0]])]});}
            var Q17;
            {var subQ0=sQuery(id+"F0.wireOp",EDGE,"E39");var subQ1=sQuery(id+"F0.wireOp",EDGE,"E29.MirrorCS");var subQ2=makeQuery(id+"F0.imprint","INTERSECT",VERTEX,{"derivedFrom":[subQ1,subQ0]});Q17=makeQuery(id+"F0.imprint","IMPRINT",FACE,{"disambiguationData":[TD([[makeQuery(id+"F0.imprint","IMPRINT",EDGE,{"disambiguationData":[TD([[subQ2,-1.0]])],"derivedFrom":subQ1}),-1.0]])]});}
            var Q18;
            {var subQ0=sQuery(id+"F0.wireOp",EDGE,"E38");var subQ1=sQuery(id+"F0.wireOp",EDGE,"E9");var subQ2=makeQuery(id+"F0.imprint","INTERSECT",VERTEX,{"derivedFrom":[subQ1,subQ0]});Q18=makeQuery(id+"F0.imprint","IMPRINT",FACE,{"disambiguationData":[TD([[makeQuery(id+"F0.imprint","IMPRINT",EDGE,{"disambiguationData":[TD([[subQ2,-1.0]])],"derivedFrom":subQ1}),1.0]])]});}
            var Q19;
            {var subQ0=sQuery(id+"F0.wireOp",EDGE,"E38");var subQ1=sQuery(id+"F0.wireOp",EDGE,"E12");var subQ2=makeQuery(id+"F0.imprint","INTERSECT",VERTEX,{"derivedFrom":[subQ1,subQ0]});Q19=makeQuery(id+"F0.imprint","IMPRINT",FACE,{"disambiguationData":[TD([[makeQuery(id+"F0.imprint","IMPRINT",EDGE,{"disambiguationData":[TD([[subQ2,-1.0]])],"derivedFrom":subQ1}),-1.0]])]});}
            var Q20;
            {var subQ0=sQuery(id+"F0.wireOp",EDGE,"E36");var subQ1=sQuery(id+"F0.wireOp",EDGE,"E32.MirrorCS");var subQ2=makeQuery(id+"F0.imprint","INTERSECT",VERTEX,{"derivedFrom":[subQ1,subQ0]});Q20=makeQuery(id+"F0.imprint","IMPRINT",FACE,{"disambiguationData":[TD([[makeQuery(id+"F0.imprint","IMPRINT",EDGE,{"disambiguationData":[TD([[subQ2,1.0]])],"derivedFrom":subQ1}),1.0]])]});}
            var Q21;
            {var subQ0=sQuery(id+"F0.wireOp",EDGE,"E40");var subQ1=sQuery(id+"F0.wireOp",EDGE,"E36");var subQ2=makeQuery(id+"F0.imprint","INTERSECT",VERTEX,{"disambiguationData":[OD(0.0)],"derivedFrom":[subQ1,subQ0]});Q21=makeQuery(id+"F0.imprint","IMPRINT",FACE,{"disambiguationData":[TD([[makeQuery(id+"F0.imprint","IMPRINT",EDGE,{"disambiguationData":[TD([[subQ2,-1.0]])],"derivedFrom":subQ1}),1.0]])]});}
            var Q22;
            {var subQ5=sQuery(id+"F0.wireOp",EDGE,"29c7e069-055f-4118-b34c-edf3fcd1c2af.sketch_text.stroke-1");Q22=makeQuery(id+"F0.imprint","IMPRINT",FACE,{"disambiguationData":[TD([[makeQuery(id+"F0.imprint","IMPRINT",EDGE,{"derivedFrom":subQ5}),1.0]])]});}
            extrude(context, id + "F3", {"entities" : qUnion([Q0, Q1, Q2, Q3, Q4, Q5, Q6, Q7, Q8, Q9, Q10, Q11, Q12, Q13, Q14, Q15, Q16, Q17, Q18, Q19, Q20, Q21, Q22]), "operationType" : NewBodyOperationType.ADD, "oppositeDirection" : true, "depth" : 5.08 * mm});
        }
        {
            var Q0;
            {var subQ0=sQuery(id+"F0.wireOp",EDGE,"E23.MirrorCS");Q0=makeQuery(id+"F0.imprint","IMPRINT",FACE,{"disambiguationData":[TD([[makeQuery(id+"F0.imprint","IMPRINT",EDGE,{"derivedFrom":subQ0}),-1.0]])]});}
            var Q1;
            {var subQ0=sQuery(id+"F0.wireOp",EDGE,"E32.MirrorCS");var subQ1=sQuery(id+"F0.wireOp",EDGE,"E22.MirrorCS");var subQ2=makeQuery(id+"F0.imprint","INTERSECT",VERTEX,{"derivedFrom":[subQ1,subQ0]});Q1=makeQuery(id+"F0.imprint","IMPRINT",FACE,{"disambiguationData":[TD([[makeQuery(id+"F0.imprint","IMPRINT",EDGE,{"disambiguationData":[TD([[subQ2,1.0]])],"derivedFrom":subQ1}),-1.0]])]});}
            var Q2;
            {var subQ0=sQuery(id+"F0.wireOp",EDGE,"E34.MirrorCS");var subQ1=sQuery(id+"F0.wireOp",EDGE,"E33.MirrorCS");var subQ2=makeQuery(id+"F0.imprint","INTERSECT",VERTEX,{"derivedFrom":[subQ1,subQ0]});Q2=makeQuery(id+"F0.imprint","IMPRINT",FACE,{"disambiguationData":[TD([[makeQuery(id+"F0.imprint","IMPRINT",EDGE,{"disambiguationData":[TD([[subQ2,1.0]])],"derivedFrom":subQ1}),1.0]])]});}
            var Q3;
            {var subQ0=sQuery(id+"F0.wireOp",EDGE,"E35.MirrorCS");Q3=makeQuery(id+"F0.imprint","IMPRINT",FACE,{"disambiguationData":[TD([[makeQuery(id+"F0.imprint","IMPRINT",EDGE,{"derivedFrom":subQ0}),1.0]])]});}
            var Q4;
            {var subQ1=sQuery(id+"F0.wireOp",EDGE,"E30.MirrorCS");Q4=makeQuery(id+"F0.imprint","IMPRINT",FACE,{"disambiguationData":[TD([[makeQuery(id+"F0.imprint","IMPRINT",EDGE,{"derivedFrom":subQ1}),-1.0]])]});}
            var Q5;
            {var subQ0=sQuery(id+"F0.wireOp",EDGE,"E12");Q5=makeQuery(id+"F0.imprint","IMPRINT",FACE,{"disambiguationData":[TD([[makeQuery(id+"F0.imprint","IMPRINT",EDGE,{"derivedFrom":subQ0}),-1.0]])]});}
            var Q6;
            {var subQ4=sQuery(id+"F0.wireOp",EDGE,"E8");Q6=makeQuery(id+"F0.imprint","IMPRINT",FACE,{"disambiguationData":[TD([[makeQuery(id+"F0.imprint","IMPRINT",EDGE,{"derivedFrom":subQ4}),1.0]])]});}
            var Q7;
            {var subQ0=sQuery(id+"F0.wireOp",EDGE,"E3");Q7=makeQuery(id+"F0.imprint","IMPRINT",FACE,{"disambiguationData":[TD([[makeQuery(id+"F0.imprint","IMPRINT",EDGE,{"derivedFrom":subQ0}),-1.0]])]});}
            var Q8;
            {var subQ0=sQuery(id+"F0.wireOp",EDGE,"E28.MirrorCS");Q8=makeQuery(id+"F0.imprint","IMPRINT",FACE,{"disambiguationData":[TD([[makeQuery(id+"F0.imprint","IMPRINT",EDGE,{"derivedFrom":subQ0}),1.0]])]});}
            var Q9;
            Q9=makeQuery(id+"F0.imprint","IMPRINT",FACE,{"disambiguationData":[TD([[makeQuery(id+"F0.imprint","IMPRINT",EDGE,{"derivedFrom":sQuery(id+"F0.wireOp",EDGE,"E2")}),1.0]])]});
            var Q10;
            {var subQ0=sQuery(id+"F0.wireOp",EDGE,"E19.MirrorCS");var subQ1=sQuery(id+"F0.wireOp",EDGE,"E0");var subQ2=makeQuery(id+"F0.imprint","INTERSECT",VERTEX,{"derivedFrom":[subQ1,subQ0]});Q10=makeQuery(id+"F0.imprint","IMPRINT",FACE,{"disambiguationData":[TD([[makeQuery(id+"F0.imprint","IMPRINT",EDGE,{"disambiguationData":[TD([[subQ2,1.0]])],"derivedFrom":subQ1}),-1.0]])]});}
            var Q11;
            {var subQ0=sQuery(id+"F0.wireOp",EDGE,"E20.MirrorCS");var subQ1=sQuery(id+"F0.wireOp",EDGE,"E1");var subQ2=makeQuery(id+"F0.imprint","INTERSECT",VERTEX,{"derivedFrom":[subQ1,subQ0]});Q11=makeQuery(id+"F0.imprint","IMPRINT",FACE,{"disambiguationData":[TD([[makeQuery(id+"F0.imprint","IMPRINT",EDGE,{"disambiguationData":[TD([[subQ2,1.0]])],"derivedFrom":subQ1}),1.0]])]});}
            var Q12;
            {var subQ0=sQuery(id+"F0.wireOp",EDGE,"E26.MirrorCS");Q12=makeQuery(id+"F0.imprint","IMPRINT",FACE,{"disambiguationData":[TD([[makeQuery(id+"F0.imprint","IMPRINT",EDGE,{"derivedFrom":subQ0}),1.0]])]});}
            var Q13;
            {var subQ0=sQuery(id+"F0.wireOp",EDGE,"E5");Q13=makeQuery(id+"F0.imprint","IMPRINT",FACE,{"disambiguationData":[TD([[makeQuery(id+"F0.imprint","IMPRINT",EDGE,{"derivedFrom":subQ0}),-1.0]])]});}
            var Q14;
            {var subQ0=sQuery(id+"F0.wireOp",EDGE,"E14");var subQ1=sQuery(id+"F0.wireOp",EDGE,"E11");var subQ2=makeQuery(id+"F0.imprint","INTERSECT",VERTEX,{"derivedFrom":[subQ1,subQ0]});Q14=makeQuery(id+"F0.imprint","IMPRINT",FACE,{"disambiguationData":[TD([[makeQuery(id+"F0.imprint","IMPRINT",EDGE,{"disambiguationData":[TD([[subQ2,-1.0]])],"derivedFrom":subQ1}),-1.0]])]});}
            var Q15;
            {var subQ0=sQuery(id+"F0.wireOp",EDGE,"E17");Q15=makeQuery(id+"F0.imprint","IMPRINT",FACE,{"disambiguationData":[TD([[makeQuery(id+"F0.imprint","IMPRINT",EDGE,{"derivedFrom":subQ0}),1.0]])]});}
            var Q16;
            {var subQ0=sQuery(id+"F0.wireOp",EDGE,"E36");var subQ1=sQuery(id+"F0.wireOp",EDGE,"E22.MirrorCS");var subQ2=makeQuery(id+"F0.imprint","INTERSECT",VERTEX,{"derivedFrom":[subQ1,subQ0]});Q16=makeQuery(id+"F0.imprint","IMPRINT",FACE,{"disambiguationData":[TD([[makeQuery(id+"F0.imprint","IMPRINT",EDGE,{"disambiguationData":[TD([[subQ2,-1.0]])],"derivedFrom":subQ1}),-1.0]])]});}
            var Q17;
            {var subQ1=sQuery(id+"F0.wireOp",EDGE,"E33.MirrorCS");var subQ7=sQuery(id+"F0.wireOp",EDGE,"E21.MirrorCS");var subQ8=makeQuery(id+"F0.imprint","INTERSECT",VERTEX,{"derivedFrom":[subQ7,subQ1]});Q17=makeQuery(id+"F0.imprint","IMPRINT",FACE,{"disambiguationData":[TD([[makeQuery(id+"F0.imprint","IMPRINT",EDGE,{"disambiguationData":[TD([[subQ8,1.0]])],"derivedFrom":subQ7}),1.0]])]});}
            var Q18;
            {var subQ0=sQuery(id+"F0.wireOp",EDGE,"E29.MirrorCS");var subQ1=sQuery(id+"F0.wireOp",EDGE,"E24.MirrorCS");var subQ2=makeQuery(id+"F0.imprint","INTERSECT",VERTEX,{"derivedFrom":[subQ1,subQ0]});Q18=makeQuery(id+"F0.imprint","IMPRINT",FACE,{"disambiguationData":[TD([[makeQuery(id+"F0.imprint","IMPRINT",EDGE,{"disambiguationData":[TD([[subQ2,-1.0]])],"derivedFrom":subQ1}),-1.0]])]});}
            var Q19;
            {var subQ0=sQuery(id+"F0.wireOp",EDGE,"E10");var subQ1=sQuery(id+"F0.wireOp",EDGE,"E7");var subQ2=makeQuery(id+"F0.imprint","INTERSECT",VERTEX,{"derivedFrom":[subQ1,subQ0]});Q19=makeQuery(id+"F0.imprint","IMPRINT",FACE,{"disambiguationData":[TD([[makeQuery(id+"F0.imprint","IMPRINT",EDGE,{"disambiguationData":[TD([[subQ2,-1.0]])],"derivedFrom":subQ1}),1.0]])]});}
            var Q20;
            {var subQ0=sQuery(id+"F0.wireOp",EDGE,"E36");var subQ1=sQuery(id+"F0.wireOp",EDGE,"E15");var subQ2=makeQuery(id+"F0.imprint","INTERSECT",VERTEX,{"derivedFrom":[subQ1,subQ0]});Q20=makeQuery(id+"F0.imprint","IMPRINT",FACE,{"disambiguationData":[TD([[makeQuery(id+"F0.imprint","IMPRINT",EDGE,{"disambiguationData":[TD([[subQ2,-1.0]])],"derivedFrom":subQ1}),1.0]])]});}
            var Q21;
            {var subQ0=sQuery(id+"F0.wireOp",EDGE,"E16");var subQ1=sQuery(id+"F0.wireOp",EDGE,"E15");var subQ2=makeQuery(id+"F0.imprint","INTERSECT",VERTEX,{"derivedFrom":[subQ1,subQ0]});Q21=makeQuery(id+"F0.imprint","IMPRINT",FACE,{"disambiguationData":[TD([[makeQuery(id+"F0.imprint","IMPRINT",EDGE,{"disambiguationData":[TD([[subQ2,1.0]])],"derivedFrom":subQ1}),1.0]])]});}
            var Q22;
            {var subQ5=sQuery(id+"F0.wireOp",EDGE,"E36");var subQ7=sQuery(id+"F0.wireOp",EDGE,"E11");var subQ8=makeQuery(id+"F0.imprint","INTERSECT",VERTEX,{"derivedFrom":[subQ7,subQ5]});Q22=makeQuery(id+"F0.imprint","IMPRINT",FACE,{"disambiguationData":[TD([[makeQuery(id+"F0.imprint","IMPRINT",EDGE,{"disambiguationData":[TD([[subQ8,-1.0]])],"derivedFrom":subQ7}),-1.0]])]});}
            var Q23;
            {var subQ7=sQuery(id+"F0.wireOp",EDGE,"E1");var subQ8=sQuery(id+"F0.wireOp",EDGE,"E0");var subQ9=makeQuery(id+"F0.imprint","INTERSECT",VERTEX,{"derivedFrom":[subQ8,subQ7]});Q23=makeQuery(id+"F0.imprint","IMPRINT",FACE,{"disambiguationData":[TD([[makeQuery(id+"F0.imprint","IMPRINT",EDGE,{"disambiguationData":[TD([[subQ9,-1.0]])],"derivedFrom":subQ8}),-1.0]])]});}
            var Q24;
            {var subQ1=sQuery(id+"F0.wireOp",EDGE,"E21.MirrorCS");var subQ7=sQuery(id+"F0.wireOp",EDGE,"E38");var subQ9=makeQuery(id+"F0.imprint","INTERSECT",VERTEX,{"derivedFrom":[subQ1,subQ7]});Q24=makeQuery(id+"F0.imprint","IMPRINT",FACE,{"disambiguationData":[TD([[makeQuery(id+"F0.imprint","IMPRINT",EDGE,{"disambiguationData":[TD([[subQ9,-1.0]])],"derivedFrom":subQ1}),1.0]])]});}
            var Q25;
            {var subQ0=sQuery(id+"F0.wireOp",EDGE,"E31.MirrorCS");Q25=makeQuery(id+"F0.imprint","IMPRINT",FACE,{"disambiguationData":[TD([[makeQuery(id+"F0.imprint","IMPRINT",EDGE,{"derivedFrom":subQ0}),-1.0]])]});}
            var Q26;
            {var subQ1=sQuery(id+"F0.wireOp",EDGE,"E11");var subQ7=sQuery(id+"F0.wireOp",EDGE,"E12");var subQ8=makeQuery(id+"F0.imprint","INTERSECT",VERTEX,{"derivedFrom":[subQ1,subQ7]});Q26=makeQuery(id+"F0.imprint","IMPRINT",FACE,{"disambiguationData":[TD([[makeQuery(id+"F0.imprint","IMPRINT",EDGE,{"disambiguationData":[TD([[subQ8,1.0]])],"derivedFrom":subQ1}),-1.0]])]});}
            var Q27;
            {var subQ0=sQuery(id+"F0.wireOp",EDGE,"E38");var subQ1=sQuery(id+"F0.wireOp",EDGE,"E12");var subQ2=makeQuery(id+"F0.imprint","INTERSECT",VERTEX,{"derivedFrom":[subQ1,subQ0]});Q27=makeQuery(id+"F0.imprint","IMPRINT",FACE,{"disambiguationData":[TD([[makeQuery(id+"F0.imprint","IMPRINT",EDGE,{"disambiguationData":[TD([[subQ2,-1.0]])],"derivedFrom":subQ1}),-1.0]])]});}
            var Q28;
            {var subQ0=sQuery(id+"F0.wireOp",EDGE,"E39");var subQ1=sQuery(id+"F0.wireOp",EDGE,"E21.MirrorCS");var subQ2=makeQuery(id+"F0.imprint","INTERSECT",VERTEX,{"derivedFrom":[subQ1,subQ0]});Q28=makeQuery(id+"F0.imprint","IMPRINT",FACE,{"disambiguationData":[TD([[makeQuery(id+"F0.imprint","IMPRINT",EDGE,{"disambiguationData":[TD([[subQ2,-1.0]])],"derivedFrom":subQ1}),1.0]])]});}
            var Q29;
            {var subQ0=sQuery(id+"F0.wireOp",EDGE,"E39");var subQ1=sQuery(id+"F0.wireOp",EDGE,"E29.MirrorCS");var subQ2=makeQuery(id+"F0.imprint","INTERSECT",VERTEX,{"derivedFrom":[subQ1,subQ0]});Q29=makeQuery(id+"F0.imprint","IMPRINT",FACE,{"disambiguationData":[TD([[makeQuery(id+"F0.imprint","IMPRINT",EDGE,{"disambiguationData":[TD([[subQ2,-1.0]])],"derivedFrom":subQ1}),-1.0]])]});}
            var Q30;
            {var subQ0=sQuery(id+"F0.wireOp",EDGE,"E38");var subQ1=sQuery(id+"F0.wireOp",EDGE,"E9");var subQ2=makeQuery(id+"F0.imprint","INTERSECT",VERTEX,{"derivedFrom":[subQ1,subQ0]});Q30=makeQuery(id+"F0.imprint","IMPRINT",FACE,{"disambiguationData":[TD([[makeQuery(id+"F0.imprint","IMPRINT",EDGE,{"disambiguationData":[TD([[subQ2,-1.0]])],"derivedFrom":subQ1}),1.0]])]});}
            var Q31;
            {var subQ0=sQuery(id+"F0.wireOp",EDGE,"E10");var subQ1=sQuery(id+"F0.wireOp",EDGE,"E9");var subQ2=makeQuery(id+"F0.imprint","INTERSECT",VERTEX,{"derivedFrom":[subQ1,subQ0]});Q31=makeQuery(id+"F0.imprint","IMPRINT",FACE,{"disambiguationData":[TD([[makeQuery(id+"F0.imprint","IMPRINT",EDGE,{"disambiguationData":[TD([[subQ2,1.0]])],"derivedFrom":subQ1}),1.0]])]});}
            var Q32;
            {var subQ0=sQuery(id+"F0.wireOp",EDGE,"E39");var subQ1=sQuery(id+"F0.wireOp",EDGE,"E2");var subQ2=makeQuery(id+"F0.imprint","INTERSECT",VERTEX,{"derivedFrom":[subQ1,subQ0]});Q32=makeQuery(id+"F0.imprint","IMPRINT",FACE,{"disambiguationData":[TD([[makeQuery(id+"F0.imprint","IMPRINT",EDGE,{"disambiguationData":[TD([[subQ2,-1.0]])],"derivedFrom":subQ1}),1.0]])]});}
            var Q33;
            Q33=makeQuery(id+"F0.imprint","IMPRINT",FACE,{"disambiguationData":[TD([[makeQuery(id+"F0.imprint","IMPRINT",EDGE,{"derivedFrom":sQuery(id+"F0.wireOp",EDGE,"E42.sketch_text.stroke-0")}),1.0]])]});
            extrude(context, id + "F4", {"entities" : qUnion([Q0, Q1, Q2, Q3, Q4, Q5, Q6, Q7, Q8, Q9, Q10, Q11, Q12, Q13, Q14, Q15, Q16, Q17, Q18, Q19, Q20, Q21, Q22, Q23, Q24, Q25, Q26, Q27, Q28, Q29, Q30, Q31, Q32, Q33]), "operationType" : NewBodyOperationType.ADD, "oppositeDirection" : true, "depth" : 5.08 * mm});
        }
        {
            var Q0;
            Q0=makeQuery(id+"F0.imprint","IMPRINT",FACE,{"disambiguationData":[TD([[makeQuery(id+"F0.imprint","IMPRINT",EDGE,{"derivedFrom":sQuery(id+"F0.wireOp",EDGE,"E41")}),-1.0]])]});
            extrude(context, id + "F5", {"entities" : qUnion([Q0]), "operationType" : NewBodyOperationType.ADD, "oppositeDirection" : true, "depth" : 5.08 * mm});
        }
        {
            var Q0;
            Q0=makeQuery(id+"F5.opExtrude","CAP_FACE",FACE,{"disambiguationData":[OSD([sQuery(id+"F0.wireOp",EDGE,"E36"),sQuery(id+"F0.wireOp",EDGE,"E40"),sQuery(id+"F0.wireOp",EDGE,"E41")])],"isStart":true});
            extrude(context, id + "F6", {"entities" : qUnion([Q0]), "operationType" : NewBodyOperationType.REMOVE, "oppositeDirection" : true, "depth" : 1.52 * mm});
        }
    });
